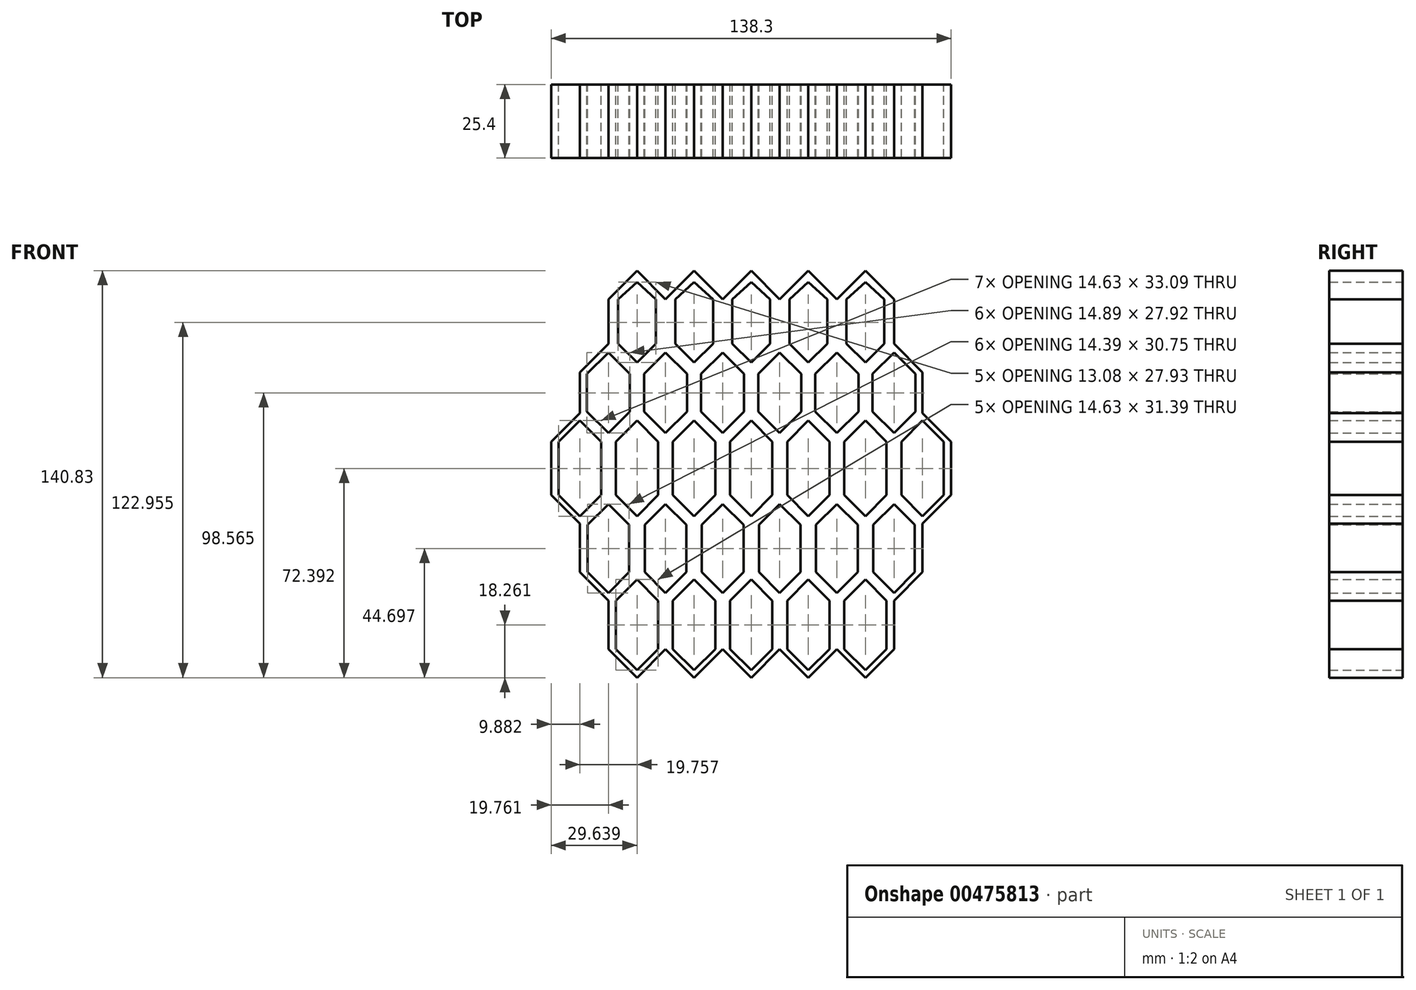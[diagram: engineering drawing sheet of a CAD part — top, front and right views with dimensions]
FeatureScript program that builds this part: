
annotation { "Feature Type Name" : "Feature", "Feature Type Description" : "" }
export const myFeature = defineFeature(function(context is Context, id is Id, definition is map)
    precondition{}
    {
        {
            var Q0;
            Q0=qCreatedBy(makeId("Front.planeOp"),FACE);
            var sketch = newSketch(context, id + "F0", { "sketchPlane" : qUnion([Q0])});
            skLineSegment(sketch, "E0", {"start": v(-42.67, 59.2) * mm, "end": v(-52.55, 49.33) * mm});
            skLineSegment(sketch, "E1", {"start": v(-52.55, 49.33) * mm, "end": v(-52.55, 33.9) * mm});
            skLineSegment(sketch, "E2", {"start": v(-52.55, 33.9) * mm, "end": v(-42.67, 24.03) * mm});
            skLineSegment(sketch, "E3", {"start": v(-42.67, 24.03) * mm, "end": v(-32.8, 33.9) * mm});
            skLineSegment(sketch, "E4", {"start": v(-32.8, 33.9) * mm, "end": v(-32.8, 49.33) * mm});
            skLineSegment(sketch, "E5", {"start": v(-32.8, 49.33) * mm, "end": v(-42.67, 59.2) * mm});
            skLineSegment(sketch, "E6", {"start": v(-32.8, 49.33) * mm, "end": v(-22.91, 59.2) * mm});
            skLineSegment(sketch, "E7", {"start": v(-22.91, 59.2) * mm, "end": v(-13.04, 49.33) * mm});
            skLineSegment(sketch, "E8", {"start": v(-13.04, 49.33) * mm, "end": v(-13.04, 33.9) * mm});
            skLineSegment(sketch, "E9", {"start": v(-13.04, 33.9) * mm, "end": v(-22.91, 24.03) * mm});
            skLineSegment(sketch, "E10", {"start": v(-22.91, 24.03) * mm, "end": v(-32.8, 33.9) * mm});
            skLineSegment(sketch, "E11", {"start": v(-13.04, 49.33) * mm, "end": v(-3.16, 59.2) * mm});
            skLineSegment(sketch, "E12", {"start": v(-3.16, 59.2) * mm, "end": v(6.72, 49.33) * mm});
            skLineSegment(sketch, "E13", {"start": v(6.72, 49.33) * mm, "end": v(6.72, 33.9) * mm});
            skLineSegment(sketch, "E14", {"start": v(6.72, 33.9) * mm, "end": v(-3.16, 24.03) * mm});
            skLineSegment(sketch, "E15", {"start": v(-3.16, 24.03) * mm, "end": v(-13.04, 33.9) * mm});
            skLineSegment(sketch, "E16", {"start": v(6.72, 49.33) * mm, "end": v(16.6, 59.2) * mm});
            skLineSegment(sketch, "E17", {"start": v(16.6, 59.2) * mm, "end": v(26.48, 49.33) * mm});
            skLineSegment(sketch, "E18", {"start": v(26.48, 49.33) * mm, "end": v(26.48, 33.9) * mm});
            skLineSegment(sketch, "E19", {"start": v(26.48, 33.9) * mm, "end": v(16.6, 24.03) * mm});
            skLineSegment(sketch, "E20", {"start": v(16.6, 24.03) * mm, "end": v(6.72, 33.9) * mm});
            skLineSegment(sketch, "E21", {"start": v(26.48, 49.33) * mm, "end": v(36.36, 59.2) * mm});
            skLineSegment(sketch, "E22", {"start": v(36.36, 59.2) * mm, "end": v(46.23, 49.33) * mm});
            skLineSegment(sketch, "E23", {"start": v(46.23, 49.33) * mm, "end": v(46.23, 33.9) * mm});
            skLineSegment(sketch, "E24", {"start": v(46.23, 33.9) * mm, "end": v(36.36, 24.03) * mm});
            skLineSegment(sketch, "E25", {"start": v(36.36, 24.03) * mm, "end": v(26.48, 33.9) * mm});
            skLineSegment(sketch, "E26", {"start": v(-42.67, 24.03) * mm, "end": v(-42.67, 9.88) * mm});
            skLineSegment(sketch, "E27", {"start": v(-42.67, 9.88) * mm, "end": v(-32.8, 0) * mm});
            skLineSegment(sketch, "E28", {"start": v(-32.8, 0) * mm, "end": v(-22.91, 9.88) * mm});
            skLineSegment(sketch, "E29", {"start": v(-22.91, 9.88) * mm, "end": v(-22.91, 24.03) * mm});
            skLineSegment(sketch, "E30", {"start": v(-3.16, 24.03) * mm, "end": v(-3.16, 9.88) * mm});
            skLineSegment(sketch, "E31", {"start": v(-3.16, 9.88) * mm, "end": v(-13.04, 0) * mm});
            skLineSegment(sketch, "E32", {"start": v(-13.04, 0) * mm, "end": v(-22.91, 9.88) * mm});
            skLineSegment(sketch, "E33", {"start": v(16.6, 24.03) * mm, "end": v(16.6, 9.88) * mm});
            skLineSegment(sketch, "E34", {"start": v(-3.16, 9.88) * mm, "end": v(6.72, 0) * mm});
            skLineSegment(sketch, "E35", {"start": v(6.72, 0) * mm, "end": v(16.6, 9.88) * mm});
            skLineSegment(sketch, "E36", {"start": v(16.6, 9.88) * mm, "end": v(26.48, 0) * mm});
            skLineSegment(sketch, "E37", {"start": v(26.48, 0) * mm, "end": v(36.36, 9.88) * mm});
            skLineSegment(sketch, "E38", {"start": v(36.36, 9.88) * mm, "end": v(36.36, 24.03) * mm});
            skLineSegment(sketch, "E39", {"start": v(46.23, 33.9) * mm, "end": v(56.11, 24.03) * mm});
            skLineSegment(sketch, "E40", {"start": v(56.11, 24.03) * mm, "end": v(56.11, 9.88) * mm});
            skLineSegment(sketch, "E41", {"start": v(56.11, 9.88) * mm, "end": v(46.23, 0) * mm});
            skLineSegment(sketch, "E42", {"start": v(46.23, 0) * mm, "end": v(36.36, 9.88) * mm});
            skLineSegment(sketch, "E43", {"start": v(-52.55, 33.9) * mm, "end": v(-62.43, 24.03) * mm});
            skLineSegment(sketch, "E44", {"start": v(-62.43, 24.03) * mm, "end": v(-62.43, 9.88) * mm});
            skLineSegment(sketch, "E45", {"start": v(-62.43, 9.88) * mm, "end": v(-52.55, 0) * mm});
            skLineSegment(sketch, "E46", {"start": v(-52.55, 0) * mm, "end": v(-42.67, 9.88) * mm});
            skLineSegment(sketch, "E47", {"start": v(-62.43, 9.88) * mm, "end": v(-72.3, 0) * mm});
            skLineSegment(sketch, "E48", {"start": v(-72.3, 0) * mm, "end": v(-72.3, -18.46) * mm});
            skLineSegment(sketch, "E49", {"start": v(-52.55, 0) * mm, "end": v(-52.55, -18.46) * mm});
            skLineSegment(sketch, "E50", {"start": v(-52.55, -18.46) * mm, "end": v(-62.43, -28.34) * mm});
            skLineSegment(sketch, "E51", {"start": v(-62.43, -28.34) * mm, "end": v(-72.3, -18.46) * mm});
            skLineSegment(sketch, "E52", {"start": v(-32.8, 0) * mm, "end": v(-32.8, -18.46) * mm});
            skLineSegment(sketch, "E53", {"start": v(-32.8, -18.46) * mm, "end": v(-42.67, -28.34) * mm});
            skLineSegment(sketch, "E54", {"start": v(-42.67, -28.34) * mm, "end": v(-52.55, -18.46) * mm});
            skLineSegment(sketch, "E55", {"start": v(-13.04, 0) * mm, "end": v(-13.04, -18.46) * mm});
            skLineSegment(sketch, "E56", {"start": v(-13.04, -18.46) * mm, "end": v(-22.91, -28.34) * mm});
            skLineSegment(sketch, "E57", {"start": v(-22.91, -28.34) * mm, "end": v(-32.8, -18.46) * mm});
            skLineSegment(sketch, "E58", {"start": v(6.72, 0) * mm, "end": v(6.72, -18.46) * mm});
            skLineSegment(sketch, "E59", {"start": v(6.72, -18.46) * mm, "end": v(-3.16, -28.34) * mm});
            skLineSegment(sketch, "E60", {"start": v(-3.16, -28.34) * mm, "end": v(-13.04, -18.46) * mm});
            skLineSegment(sketch, "E61", {"start": v(26.48, 0) * mm, "end": v(26.48, -18.46) * mm});
            skLineSegment(sketch, "E62", {"start": v(26.48, -18.46) * mm, "end": v(16.6, -28.34) * mm});
            skLineSegment(sketch, "E63", {"start": v(16.6, -28.34) * mm, "end": v(6.72, -18.46) * mm});
            skLineSegment(sketch, "E64", {"start": v(46.23, 0) * mm, "end": v(46.23, -18.46) * mm});
            skLineSegment(sketch, "E65", {"start": v(46.23, -18.46) * mm, "end": v(36.36, -28.34) * mm});
            skLineSegment(sketch, "E66", {"start": v(36.36, -28.34) * mm, "end": v(26.48, -18.46) * mm});
            skLineSegment(sketch, "E67", {"start": v(56.11, 9.88) * mm, "end": v(65.99, 0) * mm});
            skLineSegment(sketch, "E68", {"start": v(65.99, 0) * mm, "end": v(65.99, -18.46) * mm});
            skLineSegment(sketch, "E69", {"start": v(65.99, -18.46) * mm, "end": v(56.11, -28.34) * mm});
            skLineSegment(sketch, "E70", {"start": v(56.11, -28.34) * mm, "end": v(46.23, -18.46) * mm});
            skLineSegment(sketch, "E71", {"start": v(-62.43, -28.34) * mm, "end": v(-62.43, -45.1) * mm});
            skLineSegment(sketch, "E72", {"start": v(-42.67, -28.34) * mm, "end": v(-42.67, -45.1) * mm});
            skLineSegment(sketch, "E73", {"start": v(-42.67, -45.1) * mm, "end": v(-52.55, -54.98) * mm});
            skLineSegment(sketch, "E74", {"start": v(-52.55, -54.98) * mm, "end": v(-62.43, -45.1) * mm});
            skLineSegment(sketch, "E75", {"start": v(-22.91, -28.34) * mm, "end": v(-22.91, -45.1) * mm});
            skLineSegment(sketch, "E76", {"start": v(-22.91, -45.1) * mm, "end": v(-32.8, -54.98) * mm});
            skLineSegment(sketch, "E77", {"start": v(-32.8, -54.98) * mm, "end": v(-42.67, -45.1) * mm});
            skLineSegment(sketch, "E78", {"start": v(-3.16, -28.34) * mm, "end": v(-3.16, -45.1) * mm});
            skLineSegment(sketch, "E79", {"start": v(-3.16, -45.1) * mm, "end": v(-13.04, -54.98) * mm});
            skLineSegment(sketch, "E80", {"start": v(-13.04, -54.98) * mm, "end": v(-22.91, -45.1) * mm});
            skLineSegment(sketch, "E81", {"start": v(16.6, -28.34) * mm, "end": v(16.6, -45.1) * mm});
            skLineSegment(sketch, "E82", {"start": v(16.6, -45.1) * mm, "end": v(6.72, -54.98) * mm});
            skLineSegment(sketch, "E83", {"start": v(6.72, -54.98) * mm, "end": v(-3.16, -45.1) * mm});
            skLineSegment(sketch, "E84", {"start": v(36.36, -28.34) * mm, "end": v(36.36, -45.1) * mm});
            skLineSegment(sketch, "E85", {"start": v(36.36, -45.1) * mm, "end": v(26.48, -54.98) * mm});
            skLineSegment(sketch, "E86", {"start": v(26.48, -54.98) * mm, "end": v(16.6, -45.1) * mm});
            skLineSegment(sketch, "E87", {"start": v(56.11, -28.34) * mm, "end": v(56.11, -45.1) * mm});
            skLineSegment(sketch, "E88", {"start": v(56.11, -45.1) * mm, "end": v(46.23, -54.98) * mm});
            skLineSegment(sketch, "E89", {"start": v(46.23, -54.98) * mm, "end": v(36.36, -45.1) * mm});
            skLineSegment(sketch, "E90", {"start": v(-52.55, -54.98) * mm, "end": v(-52.55, -71.74) * mm});
            skLineSegment(sketch, "E91", {"start": v(-32.8, -54.98) * mm, "end": v(-32.8, -71.74) * mm});
            skLineSegment(sketch, "E92", {"start": v(-13.04, -54.98) * mm, "end": v(-13.04, -71.74) * mm});
            skLineSegment(sketch, "E93", {"start": v(-13.04, -71.74) * mm, "end": v(-22.91, -81.62) * mm});
            skLineSegment(sketch, "E94", {"start": v(-22.91, -81.62) * mm, "end": v(-32.8, -71.74) * mm});
            skLineSegment(sketch, "E95", {"start": v(-52.55, -71.74) * mm, "end": v(-42.67, -81.62) * mm});
            skLineSegment(sketch, "E96", {"start": v(-42.67, -81.62) * mm, "end": v(-32.8, -71.74) * mm});
            skLineSegment(sketch, "E97", {"start": v(6.72, -54.98) * mm, "end": v(6.72, -71.74) * mm});
            skLineSegment(sketch, "E98", {"start": v(6.72, -71.74) * mm, "end": v(-3.16, -81.62) * mm});
            skLineSegment(sketch, "E99", {"start": v(-3.16, -81.62) * mm, "end": v(-13.04, -71.74) * mm});
            skLineSegment(sketch, "E100", {"start": v(26.48, -54.98) * mm, "end": v(26.48, -71.74) * mm});
            skLineSegment(sketch, "E101", {"start": v(26.48, -71.74) * mm, "end": v(16.6, -81.62) * mm});
            skLineSegment(sketch, "E102", {"start": v(16.6, -81.62) * mm, "end": v(6.72, -71.74) * mm});
            skLineSegment(sketch, "E103", {"start": v(46.23, -54.98) * mm, "end": v(46.23, -71.74) * mm});
            skLineSegment(sketch, "E104", {"start": v(46.23, -71.74) * mm, "end": v(36.36, -81.62) * mm});
            skLineSegment(sketch, "E105", {"start": v(36.36, -81.62) * mm, "end": v(26.48, -71.74) * mm});
            skLineSegment(sketch, "E106", {"start": v(-49.21, 49.33) * mm, "end": v(-49.21, 33.9) * mm});
            skLineSegment(sketch, "E107", {"start": v(-49.21, 33.9) * mm, "end": v(-42.67, 27.37) * mm});
            skPoint(sketch, "E107.endSnap0", {"position": v(-42.67, 16.95) * mm});
            skLineSegment(sketch, "E108", {"start": v(-42.67, 55.3) * mm, "end": v(-49.21, 49.33) * mm});
            skLineSegment(sketch, "E109.MirrorCS", {"start": v(-42.67, 55.3) * mm, "end": v(-36.13, 49.33) * mm});
            skLineSegment(sketch, "E110.MirrorCS", {"start": v(-36.13, 49.33) * mm, "end": v(-36.13, 33.9) * mm});
            skLineSegment(sketch, "E111.MirrorCS", {"start": v(-36.13, 33.9) * mm, "end": v(-42.67, 27.37) * mm});
            skLineSegment(sketch, "E112.MirrorCS", {"start": v(-29.46, 49.33) * mm, "end": v(-29.46, 33.9) * mm});
            skLineSegment(sketch, "E113.MirrorCS", {"start": v(-22.91, 55.3) * mm, "end": v(-29.46, 49.33) * mm});
            skLineSegment(sketch, "E114.MirrorCS", {"start": v(-22.91, 55.3) * mm, "end": v(-16.37, 49.33) * mm});
            skLineSegment(sketch, "E115.MirrorCS", {"start": v(-16.37, 49.33) * mm, "end": v(-16.37, 33.9) * mm});
            skLineSegment(sketch, "E116.MirrorCS", {"start": v(-16.37, 33.9) * mm, "end": v(-22.91, 27.37) * mm});
            skLineSegment(sketch, "E117.MirrorCS", {"start": v(-29.46, 33.9) * mm, "end": v(-22.91, 27.37) * mm});
            skLineSegment(sketch, "E118.MirrorCS", {"start": v(-9.7, 49.33) * mm, "end": v(-9.7, 33.9) * mm});
            skLineSegment(sketch, "E119.MirrorCS", {"start": v(3.38, 49.33) * mm, "end": v(3.38, 33.9) * mm});
            skLineSegment(sketch, "E120.MirrorCS", {"start": v(-3.16, 55.3) * mm, "end": v(3.38, 49.33) * mm});
            skLineSegment(sketch, "E121.MirrorCS", {"start": v(-3.16, 55.3) * mm, "end": v(-9.7, 49.33) * mm});
            skLineSegment(sketch, "E122.MirrorCS", {"start": v(3.38, 33.9) * mm, "end": v(-3.16, 27.37) * mm});
            skLineSegment(sketch, "E123.MirrorCS", {"start": v(-9.7, 33.9) * mm, "end": v(-3.16, 27.37) * mm});
            skLineSegment(sketch, "E124.MirrorCS", {"start": v(10.06, 49.33) * mm, "end": v(10.06, 33.9) * mm});
            skLineSegment(sketch, "E125.MirrorCS", {"start": v(16.6, 55.3) * mm, "end": v(10.06, 49.33) * mm});
            skLineSegment(sketch, "E126.MirrorCS", {"start": v(16.6, 55.3) * mm, "end": v(23.14, 49.33) * mm});
            skLineSegment(sketch, "E127.MirrorCS", {"start": v(23.14, 49.33) * mm, "end": v(23.14, 33.9) * mm});
            skLineSegment(sketch, "E128.MirrorCS", {"start": v(23.14, 33.9) * mm, "end": v(16.6, 27.37) * mm});
            skLineSegment(sketch, "E129.MirrorCS", {"start": v(10.06, 33.9) * mm, "end": v(16.6, 27.37) * mm});
            skLineSegment(sketch, "E130.MirrorCS", {"start": v(29.81, 49.33) * mm, "end": v(29.81, 33.9) * mm});
            skLineSegment(sketch, "E131.MirrorCS", {"start": v(42.9, 49.33) * mm, "end": v(42.9, 33.9) * mm});
            skLineSegment(sketch, "E132.MirrorCS", {"start": v(36.36, 55.3) * mm, "end": v(42.9, 49.33) * mm});
            skLineSegment(sketch, "E133.MirrorCS", {"start": v(36.36, 55.3) * mm, "end": v(29.81, 49.33) * mm});
            skLineSegment(sketch, "E134.MirrorCS", {"start": v(29.81, 33.9) * mm, "end": v(36.36, 27.37) * mm});
            skLineSegment(sketch, "E135.MirrorCS", {"start": v(42.9, 33.9) * mm, "end": v(36.36, 27.37) * mm});
            skLineSegment(sketch, "E136", {"start": v(-40.24, 23.46) * mm, "end": v(-40.24, 10.43) * mm});
            skLineSegment(sketch, "E137", {"start": v(-40.24, 10.43) * mm, "end": v(-32.8, 2.99) * mm});
            skLineSegment(sketch, "E138", {"start": v(-40.24, 23.46) * mm, "end": v(-32.8, 30.9) * mm});
            skLineSegment(sketch, "E139.MirrorCS", {"start": v(-25.35, 23.46) * mm, "end": v(-32.8, 30.9) * mm});
            skPoint(sketch, "E140.MirrorP", {"position": v(-22.91, 16.95) * mm});
            skLineSegment(sketch, "E141.MirrorCS", {"start": v(-25.35, 10.43) * mm, "end": v(-32.8, 2.99) * mm});
            skLineSegment(sketch, "E142.MirrorCS", {"start": v(-25.35, 23.46) * mm, "end": v(-25.35, 10.43) * mm});
            skLineSegment(sketch, "E143.MirrorCS", {"start": v(-45.1, 23.46) * mm, "end": v(-52.55, 30.9) * mm});
            skLineSegment(sketch, "E144.MirrorCS", {"start": v(-60, 23.46) * mm, "end": v(-52.55, 30.9) * mm});
            skPoint(sketch, "E145.MirrorP", {"position": v(-62.43, 16.95) * mm});
            skLineSegment(sketch, "E146.MirrorCS", {"start": v(-60, 23.46) * mm, "end": v(-60, 10.43) * mm});
            skLineSegment(sketch, "E147.MirrorCS", {"start": v(-60, 10.43) * mm, "end": v(-52.55, 2.99) * mm});
            skLineSegment(sketch, "E148.MirrorCS", {"start": v(-45.1, 10.43) * mm, "end": v(-52.55, 2.99) * mm});
            skLineSegment(sketch, "E149.MirrorCS", {"start": v(-45.1, 23.46) * mm, "end": v(-45.1, 10.43) * mm});
            skLineSegment(sketch, "E150.MirrorCS", {"start": v(-20.48, 23.46) * mm, "end": v(-20.48, 10.43) * mm});
            skLineSegment(sketch, "E151.MirrorCS", {"start": v(-5.6, 23.46) * mm, "end": v(-5.6, 10.43) * mm});
            skLineSegment(sketch, "E152.MirrorCS", {"start": v(-5.6, 23.46) * mm, "end": v(-13.04, 30.9) * mm});
            skLineSegment(sketch, "E153.MirrorCS", {"start": v(-20.48, 23.46) * mm, "end": v(-13.04, 30.9) * mm});
            skLineSegment(sketch, "E154.MirrorCS", {"start": v(-20.48, 10.43) * mm, "end": v(-13.04, 2.99) * mm});
            skLineSegment(sketch, "E155.MirrorCS", {"start": v(-5.6, 10.43) * mm, "end": v(-13.04, 2.99) * mm});
            skLineSegment(sketch, "E156.MirrorCS", {"start": v(-0.72, 23.46) * mm, "end": v(-0.72, 10.43) * mm});
            skLineSegment(sketch, "E157.MirrorCS", {"start": v(14.17, 23.46) * mm, "end": v(14.17, 10.43) * mm});
            skLineSegment(sketch, "E158.MirrorCS", {"start": v(14.17, 23.46) * mm, "end": v(6.72, 30.9) * mm});
            skLineSegment(sketch, "E159.MirrorCS", {"start": v(-0.72, 23.46) * mm, "end": v(6.72, 30.9) * mm});
            skLineSegment(sketch, "E160.MirrorCS", {"start": v(-0.72, 10.43) * mm, "end": v(6.72, 2.99) * mm});
            skLineSegment(sketch, "E161.MirrorCS", {"start": v(14.17, 10.43) * mm, "end": v(6.72, 2.99) * mm});
            skLineSegment(sketch, "E162.MirrorCS", {"start": v(19.03, 23.46) * mm, "end": v(19.03, 10.43) * mm});
            skLineSegment(sketch, "E163.MirrorCS", {"start": v(33.92, 23.46) * mm, "end": v(33.92, 10.43) * mm});
            skLineSegment(sketch, "E164.MirrorCS", {"start": v(33.92, 23.46) * mm, "end": v(26.48, 30.9) * mm});
            skLineSegment(sketch, "E165.MirrorCS", {"start": v(19.03, 23.46) * mm, "end": v(26.48, 30.9) * mm});
            skLineSegment(sketch, "E166.MirrorCS", {"start": v(19.03, 10.43) * mm, "end": v(26.48, 2.99) * mm});
            skLineSegment(sketch, "E167.MirrorCS", {"start": v(33.92, 10.43) * mm, "end": v(26.48, 2.99) * mm});
            skLineSegment(sketch, "E168.MirrorCS", {"start": v(38.79, 23.46) * mm, "end": v(38.79, 10.43) * mm});
            skLineSegment(sketch, "E169.MirrorCS", {"start": v(53.68, 23.46) * mm, "end": v(53.68, 10.43) * mm});
            skLineSegment(sketch, "E170.MirrorCS", {"start": v(53.68, 23.46) * mm, "end": v(46.23, 30.9) * mm});
            skLineSegment(sketch, "E171.MirrorCS", {"start": v(38.79, 23.46) * mm, "end": v(46.23, 30.9) * mm});
            skLineSegment(sketch, "E172.MirrorCS", {"start": v(38.79, 10.43) * mm, "end": v(46.23, 2.99) * mm});
            skLineSegment(sketch, "E173.MirrorCS", {"start": v(53.68, 10.43) * mm, "end": v(46.23, 2.99) * mm});
            skLineSegment(sketch, "E174", {"start": v(-49.99, 0) * mm, "end": v(-49.99, -18.46) * mm});
            skLineSegment(sketch, "E175", {"start": v(-49.99, -18.46) * mm, "end": v(-42.67, -25.77) * mm});
            skLineSegment(sketch, "E176", {"start": v(-49.99, 0) * mm, "end": v(-42.67, 7.31) * mm});
            skLineSegment(sketch, "E177.MirrorCS", {"start": v(-35.36, 0) * mm, "end": v(-42.67, 7.31) * mm});
            skLineSegment(sketch, "E178.MirrorCS", {"start": v(-35.36, 0) * mm, "end": v(-35.36, -18.46) * mm});
            skLineSegment(sketch, "E179.MirrorCS", {"start": v(-35.36, -18.46) * mm, "end": v(-42.67, -25.77) * mm});
            skLineSegment(sketch, "E180.MirrorCS", {"start": v(-55.11, 0) * mm, "end": v(-55.11, -18.46) * mm});
            skLineSegment(sketch, "E181.MirrorCS", {"start": v(-69.74, 0) * mm, "end": v(-62.43, 7.31) * mm});
            skLineSegment(sketch, "E182.MirrorCS", {"start": v(-55.11, 0) * mm, "end": v(-62.43, 7.31) * mm});
            skLineSegment(sketch, "E183.MirrorCS", {"start": v(-69.74, 0) * mm, "end": v(-69.74, -18.46) * mm});
            skLineSegment(sketch, "E184.MirrorCS", {"start": v(-69.74, -18.46) * mm, "end": v(-62.43, -25.77) * mm});
            skLineSegment(sketch, "E185.MirrorCS", {"start": v(-55.11, -18.46) * mm, "end": v(-62.43, -25.77) * mm});
            skLineSegment(sketch, "E186.MirrorCS", {"start": v(-30.23, 0) * mm, "end": v(-30.23, -18.46) * mm});
            skLineSegment(sketch, "E187.MirrorCS", {"start": v(-15.6, 0) * mm, "end": v(-15.6, -18.46) * mm});
            skLineSegment(sketch, "E188.MirrorCS", {"start": v(-15.6, 0) * mm, "end": v(-22.91, 7.31) * mm});
            skLineSegment(sketch, "E189.MirrorCS", {"start": v(-30.23, 0) * mm, "end": v(-22.91, 7.31) * mm});
            skLineSegment(sketch, "E190.MirrorCS", {"start": v(-30.23, -18.46) * mm, "end": v(-22.91, -25.77) * mm});
            skLineSegment(sketch, "E191.MirrorCS", {"start": v(-15.6, -18.46) * mm, "end": v(-22.91, -25.77) * mm});
            skLineSegment(sketch, "E192.MirrorCS", {"start": v(-10.47, 0) * mm, "end": v(-10.47, -18.46) * mm});
            skLineSegment(sketch, "E193.MirrorCS", {"start": v(-10.47, 0) * mm, "end": v(-3.16, 7.31) * mm});
            skLineSegment(sketch, "E194.MirrorCS", {"start": v(4.16, 0) * mm, "end": v(-3.16, 7.31) * mm});
            skLineSegment(sketch, "E195.MirrorCS", {"start": v(4.16, 0) * mm, "end": v(4.16, -18.46) * mm});
            skLineSegment(sketch, "E196.MirrorCS", {"start": v(4.16, -18.46) * mm, "end": v(-3.16, -25.77) * mm});
            skLineSegment(sketch, "E197.MirrorCS", {"start": v(-10.47, -18.46) * mm, "end": v(-3.16, -25.77) * mm});
            skLineSegment(sketch, "E198.MirrorCS", {"start": v(9.28, 0) * mm, "end": v(9.28, -18.46) * mm});
            skLineSegment(sketch, "E199.MirrorCS", {"start": v(23.91, 0) * mm, "end": v(23.91, -18.46) * mm});
            skLineSegment(sketch, "E200.MirrorCS", {"start": v(23.91, 0) * mm, "end": v(16.6, 7.31) * mm});
            skLineSegment(sketch, "E201.MirrorCS", {"start": v(9.28, 0) * mm, "end": v(16.6, 7.31) * mm});
            skLineSegment(sketch, "E202.MirrorCS", {"start": v(9.28, -18.46) * mm, "end": v(16.6, -25.77) * mm});
            skLineSegment(sketch, "E203.MirrorCS", {"start": v(23.91, -18.46) * mm, "end": v(16.6, -25.77) * mm});
            skLineSegment(sketch, "E204.MirrorCS", {"start": v(29.04, 0) * mm, "end": v(29.04, -18.46) * mm});
            skLineSegment(sketch, "E205.MirrorCS", {"start": v(43.67, 0) * mm, "end": v(43.67, -18.46) * mm});
            skLineSegment(sketch, "E206.MirrorCS", {"start": v(43.67, 0) * mm, "end": v(36.36, 7.31) * mm});
            skLineSegment(sketch, "E207.MirrorCS", {"start": v(29.04, 0) * mm, "end": v(36.36, 7.31) * mm});
            skLineSegment(sketch, "E208.MirrorCS", {"start": v(29.04, -18.46) * mm, "end": v(36.36, -25.77) * mm});
            skLineSegment(sketch, "E209.MirrorCS", {"start": v(43.67, -18.46) * mm, "end": v(36.36, -25.77) * mm});
            skLineSegment(sketch, "E210.MirrorCS", {"start": v(36.36, 9.88) * mm, "end": v(46.23, 0) * mm});
            skLineSegment(sketch, "E211.MirrorCS", {"start": v(36.36, 9.88) * mm, "end": v(26.48, 0) * mm});
            skLineSegment(sketch, "E212.MirrorCS", {"start": v(26.48, -18.46) * mm, "end": v(36.36, -28.34) * mm});
            skLineSegment(sketch, "E213.MirrorCS", {"start": v(48.8, 0) * mm, "end": v(48.8, -18.46) * mm});
            skLineSegment(sketch, "E214.MirrorCS", {"start": v(48.8, 0) * mm, "end": v(56.11, 7.31) * mm});
            skLineSegment(sketch, "E215.MirrorCS", {"start": v(63.43, 0) * mm, "end": v(56.11, 7.31) * mm});
            skLineSegment(sketch, "E216.MirrorCS", {"start": v(63.43, 0) * mm, "end": v(63.43, -18.46) * mm});
            skLineSegment(sketch, "E217.MirrorCS", {"start": v(63.43, -18.46) * mm, "end": v(56.11, -25.77) * mm});
            skLineSegment(sketch, "E218.MirrorCS", {"start": v(48.8, -18.46) * mm, "end": v(56.11, -25.77) * mm});
            skLineSegment(sketch, "E219", {"start": v(-59.75, -28.75) * mm, "end": v(-59.75, -45.1) * mm});
            skLineSegment(sketch, "E220", {"start": v(-59.75, -45.1) * mm, "end": v(-52.55, -52.3) * mm});
            skLineSegment(sketch, "E221", {"start": v(-59.75, -28.75) * mm, "end": v(-52.55, -21.55) * mm});
            skLineSegment(sketch, "E222.MirrorCS", {"start": v(-45.35, -28.75) * mm, "end": v(-52.55, -21.55) * mm});
            skLineSegment(sketch, "E223.MirrorCS", {"start": v(-45.35, -28.75) * mm, "end": v(-45.35, -45.1) * mm});
            skLineSegment(sketch, "E224.MirrorCS", {"start": v(-45.35, -45.1) * mm, "end": v(-52.55, -52.3) * mm});
            skLineSegment(sketch, "E225.MirrorCS", {"start": v(-39.99, -28.75) * mm, "end": v(-39.99, -45.1) * mm});
            skLineSegment(sketch, "E226.MirrorCS", {"start": v(-39.99, -28.75) * mm, "end": v(-32.8, -21.55) * mm});
            skLineSegment(sketch, "E227.MirrorCS", {"start": v(-39.99, -45.1) * mm, "end": v(-32.8, -52.3) * mm});
            skLineSegment(sketch, "E228.MirrorCS", {"start": v(-25.6, -45.1) * mm, "end": v(-32.8, -52.3) * mm});
            skLineSegment(sketch, "E229.MirrorCS", {"start": v(-25.6, -28.75) * mm, "end": v(-25.6, -45.1) * mm});
            skLineSegment(sketch, "E230.MirrorCS", {"start": v(-25.6, -28.75) * mm, "end": v(-32.8, -21.55) * mm});
            skLineSegment(sketch, "E231.MirrorCS", {"start": v(-20.23, -28.75) * mm, "end": v(-20.23, -45.1) * mm});
            skLineSegment(sketch, "E232.MirrorCS", {"start": v(-20.23, -28.75) * mm, "end": v(-13.04, -21.55) * mm});
            skLineSegment(sketch, "E233.MirrorCS", {"start": v(-5.84, -28.75) * mm, "end": v(-13.04, -21.55) * mm});
            skLineSegment(sketch, "E234.MirrorCS", {"start": v(-5.84, -28.75) * mm, "end": v(-5.84, -45.1) * mm});
            skLineSegment(sketch, "E235.MirrorCS", {"start": v(-5.84, -45.1) * mm, "end": v(-13.04, -52.3) * mm});
            skLineSegment(sketch, "E236.MirrorCS", {"start": v(-20.23, -45.1) * mm, "end": v(-13.04, -52.3) * mm});
            skLineSegment(sketch, "E237.MirrorCS", {"start": v(-0.48, -28.75) * mm, "end": v(-0.48, -45.1) * mm});
            skLineSegment(sketch, "E238.MirrorCS", {"start": v(-0.48, -28.75) * mm, "end": v(6.72, -21.55) * mm});
            skLineSegment(sketch, "E239.MirrorCS", {"start": v(13.92, -28.75) * mm, "end": v(6.72, -21.55) * mm});
            skLineSegment(sketch, "E240.MirrorCS", {"start": v(13.92, -28.75) * mm, "end": v(13.92, -45.1) * mm});
            skLineSegment(sketch, "E241.MirrorCS", {"start": v(13.92, -45.1) * mm, "end": v(6.72, -52.3) * mm});
            skLineSegment(sketch, "E242.MirrorCS", {"start": v(-0.48, -45.1) * mm, "end": v(6.72, -52.3) * mm});
            skLineSegment(sketch, "E243.MirrorCS", {"start": v(19.28, -28.75) * mm, "end": v(19.28, -45.1) * mm});
            skLineSegment(sketch, "E244.MirrorCS", {"start": v(19.28, -28.75) * mm, "end": v(26.48, -21.55) * mm});
            skLineSegment(sketch, "E245.MirrorCS", {"start": v(33.67, -28.75) * mm, "end": v(26.48, -21.55) * mm});
            skLineSegment(sketch, "E246.MirrorCS", {"start": v(33.67, -28.75) * mm, "end": v(33.67, -45.1) * mm});
            skLineSegment(sketch, "E247.MirrorCS", {"start": v(33.67, -45.1) * mm, "end": v(26.48, -52.3) * mm});
            skLineSegment(sketch, "E248.MirrorCS", {"start": v(19.28, -45.1) * mm, "end": v(26.48, -52.3) * mm});
            skLineSegment(sketch, "E249.MirrorCS", {"start": v(39.04, -28.75) * mm, "end": v(46.23, -21.55) * mm});
            skLineSegment(sketch, "E250.MirrorCS", {"start": v(39.04, -28.75) * mm, "end": v(39.04, -45.1) * mm});
            skLineSegment(sketch, "E251.MirrorCS", {"start": v(39.04, -45.1) * mm, "end": v(46.23, -52.3) * mm});
            skLineSegment(sketch, "E252.MirrorCS", {"start": v(53.43, -45.1) * mm, "end": v(46.23, -52.3) * mm});
            skLineSegment(sketch, "E253.MirrorCS", {"start": v(53.43, -28.75) * mm, "end": v(53.43, -45.1) * mm});
            skLineSegment(sketch, "E254.MirrorCS", {"start": v(53.43, -28.75) * mm, "end": v(46.23, -21.55) * mm});
            skLineSegment(sketch, "E255", {"start": v(-49.99, -71.74) * mm, "end": v(-42.67, -79.06) * mm});
            skLineSegment(sketch, "E256", {"start": v(-49.99, -54.98) * mm, "end": v(-42.67, -47.66) * mm});
            skLineSegment(sketch, "E257.MirrorCS", {"start": v(-35.36, -54.98) * mm, "end": v(-42.67, -47.66) * mm});
            skLineSegment(sketch, "E258.MirrorCS", {"start": v(-35.36, -54.98) * mm, "end": v(-35.36, -71.74) * mm});
            skLineSegment(sketch, "E259.MirrorCS", {"start": v(-35.36, -71.74) * mm, "end": v(-42.67, -79.06) * mm});
            skLineSegment(sketch, "E260.MirrorCS", {"start": v(-30.23, -54.98) * mm, "end": v(-30.23, -71.74) * mm});
            skLineSegment(sketch, "E261.MirrorCS", {"start": v(-30.23, -54.98) * mm, "end": v(-22.91, -47.66) * mm});
            skLineSegment(sketch, "E262.MirrorCS", {"start": v(-15.6, -54.98) * mm, "end": v(-22.91, -47.66) * mm});
            skLineSegment(sketch, "E263.MirrorCS", {"start": v(-15.6, -54.98) * mm, "end": v(-15.6, -71.74) * mm});
            skLineSegment(sketch, "E264.MirrorCS", {"start": v(-15.6, -71.74) * mm, "end": v(-22.91, -79.06) * mm});
            skLineSegment(sketch, "E265.MirrorCS", {"start": v(-10.47, -54.98) * mm, "end": v(-10.47, -71.74) * mm});
            skLineSegment(sketch, "E266.MirrorCS", {"start": v(-10.47, -54.98) * mm, "end": v(-3.16, -47.66) * mm});
            skLineSegment(sketch, "E267.MirrorCS", {"start": v(4.16, -54.98) * mm, "end": v(-3.16, -47.66) * mm});
            skLineSegment(sketch, "E268.MirrorCS", {"start": v(-30.23, -71.74) * mm, "end": v(-22.91, -79.06) * mm});
            skLineSegment(sketch, "E269.MirrorCS", {"start": v(-10.47, -71.74) * mm, "end": v(-3.16, -79.06) * mm});
            skLineSegment(sketch, "E270.MirrorCS", {"start": v(4.16, -71.74) * mm, "end": v(-3.16, -79.06) * mm});
            skLineSegment(sketch, "E271.MirrorCS", {"start": v(4.16, -54.98) * mm, "end": v(4.16, -71.74) * mm});
            skLineSegment(sketch, "E272.MirrorCS", {"start": v(9.28, -54.98) * mm, "end": v(9.28, -71.74) * mm});
            skLineSegment(sketch, "E273.MirrorCS", {"start": v(9.28, -54.98) * mm, "end": v(16.6, -47.66) * mm});
            skLineSegment(sketch, "E274.MirrorCS", {"start": v(23.91, -54.98) * mm, "end": v(16.6, -47.66) * mm});
            skLineSegment(sketch, "E275.MirrorCS", {"start": v(23.91, -54.98) * mm, "end": v(23.91, -71.74) * mm});
            skLineSegment(sketch, "E276.MirrorCS", {"start": v(23.91, -71.74) * mm, "end": v(16.6, -79.06) * mm});
            skLineSegment(sketch, "E277.MirrorCS", {"start": v(9.28, -71.74) * mm, "end": v(16.6, -79.06) * mm});
            skLineSegment(sketch, "E278.MirrorCS", {"start": v(29.04, -54.98) * mm, "end": v(29.04, -71.74) * mm});
            skLineSegment(sketch, "E279.MirrorCS", {"start": v(29.04, -54.98) * mm, "end": v(36.36, -47.66) * mm});
            skLineSegment(sketch, "E280.MirrorCS", {"start": v(43.67, -54.98) * mm, "end": v(36.36, -47.66) * mm});
            skLineSegment(sketch, "E281.MirrorCS", {"start": v(43.67, -54.98) * mm, "end": v(43.67, -71.74) * mm});
            skLineSegment(sketch, "E282.MirrorCS", {"start": v(43.67, -71.74) * mm, "end": v(36.36, -79.06) * mm});
            skLineSegment(sketch, "E283.MirrorCS", {"start": v(29.04, -71.74) * mm, "end": v(36.36, -79.06) * mm});
            skLineSegment(sketch, "E284", {"start": v(-49.99, -54.98) * mm, "end": v(-49.99, -71.74) * mm});
            skSolve(sketch);
        }
        {
            var Q0;
            Q0 = qSketchRegion(id + "F0", true);
            extrude(context, id + "F1", {"entities" : qUnion([Q0]), "depth" : 25.4 * mm});
        }
        {
            var Q0;
            Q0=makeQuery(id+"F0.imprint","IMPRINT",FACE,{"disambiguationData":[TD([[makeQuery(id+"F0.imprint","IMPRINT",EDGE,{"derivedFrom":sQuery(id+"F0.wireOp",EDGE,"E3")}),-1.0]])]});
            var Q1;
            Q1=makeQuery(id+"F0.imprint","IMPRINT",FACE,{"disambiguationData":[TD([[makeQuery(id+"F0.imprint","IMPRINT",EDGE,{"derivedFrom":sQuery(id+"F0.wireOp",EDGE,"E9")}),1.0]])]});
            var Q2;
            Q2=makeQuery(id+"F0.imprint","IMPRINT",FACE,{"disambiguationData":[TD([[makeQuery(id+"F0.imprint","IMPRINT",EDGE,{"derivedFrom":sQuery(id+"F0.wireOp",EDGE,"E28")}),-1.0]])]});
            var Q3;
            Q3=makeQuery(id+"F0.imprint","IMPRINT",FACE,{"disambiguationData":[TD([[makeQuery(id+"F0.imprint","IMPRINT",EDGE,{"derivedFrom":sQuery(id+"F0.wireOp",EDGE,"E31")}),1.0]])]});
            var Q4;
            Q4=makeQuery(id+"F0.imprint","IMPRINT",FACE,{"disambiguationData":[TD([[makeQuery(id+"F0.imprint","IMPRINT",EDGE,{"derivedFrom":sQuery(id+"F0.wireOp",EDGE,"E14")}),1.0]])]});
            var Q5;
            Q5=makeQuery(id+"F0.imprint","IMPRINT",FACE,{"disambiguationData":[TD([[makeQuery(id+"F0.imprint","IMPRINT",EDGE,{"derivedFrom":sQuery(id+"F0.wireOp",EDGE,"E19")}),1.0]])]});
            var Q6;
            Q6=makeQuery(id+"F0.imprint","IMPRINT",FACE,{"disambiguationData":[TD([[makeQuery(id+"F0.imprint","IMPRINT",EDGE,{"derivedFrom":sQuery(id+"F0.wireOp",EDGE,"E64")}),-1.0]])]});
            var Q7;
            Q7=makeQuery(id+"F0.imprint","IMPRINT",FACE,{"disambiguationData":[TD([[makeQuery(id+"F0.imprint","IMPRINT",EDGE,{"derivedFrom":sQuery(id+"F0.wireOp",EDGE,"E35")}),-1.0]])]});
            var Q8;
            Q8=makeQuery(id+"F0.imprint","IMPRINT",FACE,{"disambiguationData":[TD([[makeQuery(id+"F0.imprint","IMPRINT",EDGE,{"derivedFrom":sQuery(id+"F0.wireOp",EDGE,"E59")}),1.0]])]});
            var Q9;
            Q9=makeQuery(id+"F0.imprint","IMPRINT",FACE,{"disambiguationData":[TD([[makeQuery(id+"F0.imprint","IMPRINT",EDGE,{"derivedFrom":sQuery(id+"F0.wireOp",EDGE,"E56")}),1.0]])]});
            var Q10;
            Q10=makeQuery(id+"F0.imprint","IMPRINT",FACE,{"disambiguationData":[TD([[makeQuery(id+"F0.imprint","IMPRINT",EDGE,{"derivedFrom":sQuery(id+"F0.wireOp",EDGE,"E53")}),1.0]])]});
            var Q11;
            Q11=makeQuery(id+"F0.imprint","IMPRINT",FACE,{"disambiguationData":[TD([[makeQuery(id+"F0.imprint","IMPRINT",EDGE,{"derivedFrom":sQuery(id+"F0.wireOp",EDGE,"E27")}),-1.0]])]});
            var Q12;
            Q12=makeQuery(id+"F0.imprint","IMPRINT",FACE,{"disambiguationData":[TD([[makeQuery(id+"F0.imprint","IMPRINT",EDGE,{"derivedFrom":sQuery(id+"F0.wireOp",EDGE,"E62")}),1.0]])]});
            extrude(context, id + "F2", {"entities" : qUnion([Q0, Q1, Q2, Q3, Q4, Q5, Q6, Q7, Q8, Q9, Q10, Q11, Q12]), "operationType" : NewBodyOperationType.ADD, "depth" : 25.4 * mm});
        }
    });
